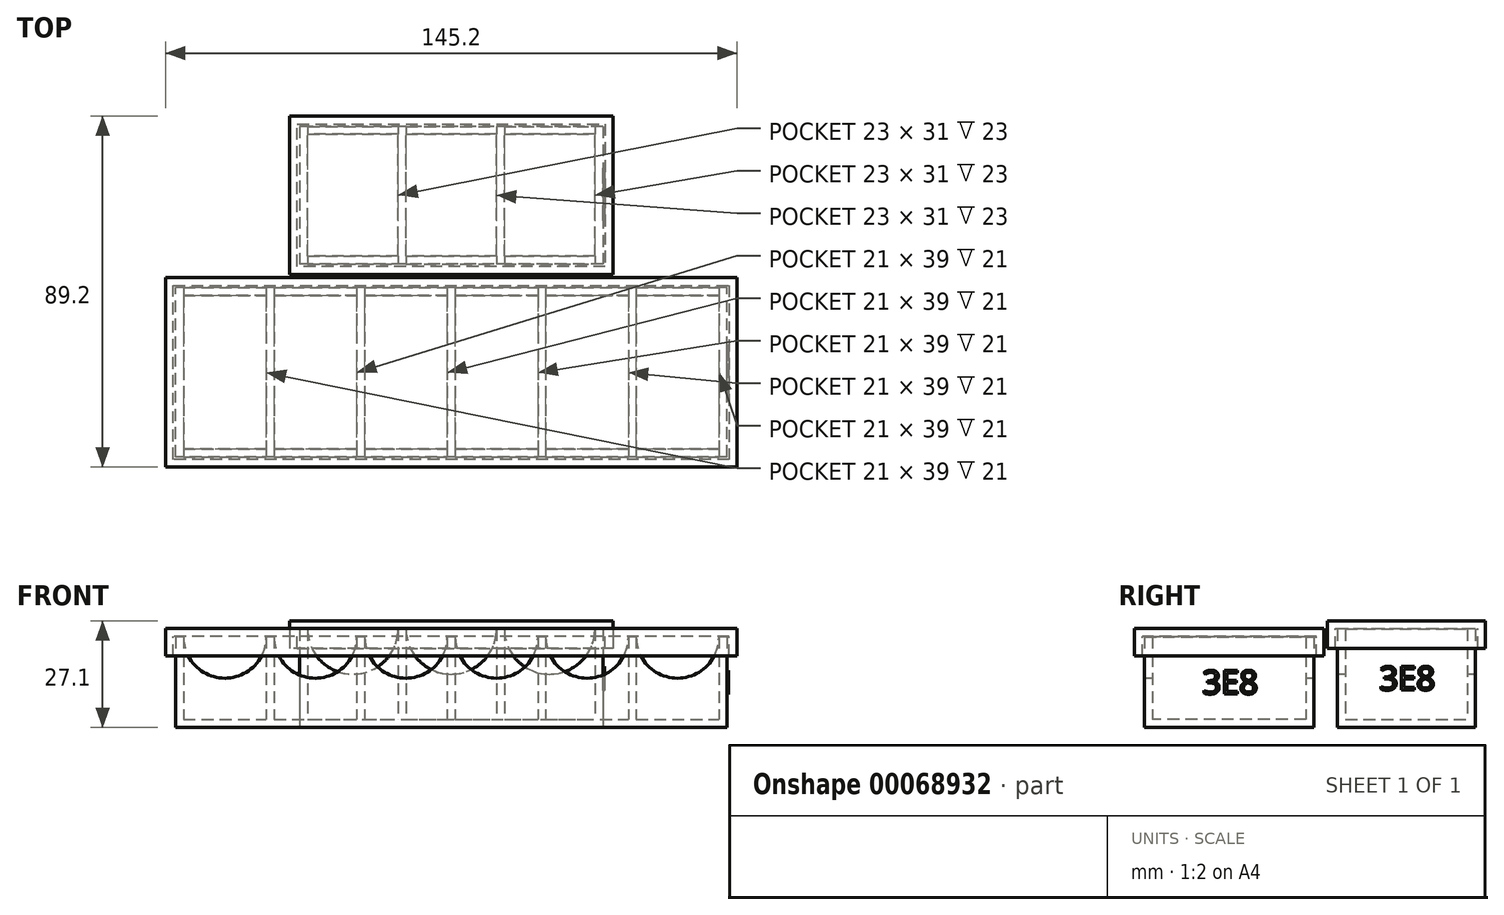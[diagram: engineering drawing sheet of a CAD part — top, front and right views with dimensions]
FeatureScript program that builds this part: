
annotation { "Feature Type Name" : "Feature", "Feature Type Description" : "" }
export const myFeature = defineFeature(function(context is Context, id is Id, definition is map)
    precondition{}
    {
        {
            var Q0;
            Q0=qCreatedBy(makeId("Top.planeOp"),FACE);
            var sketch = newSketch(context, id + "F0", { "sketchPlane" : qUnion([Q0])});
            skLineSegment(sketch, "E0.rect.bottom", {"start": v(70, -21.5) * mm, "end": v(-70, -21.5) * mm});
            skLineSegment(sketch, "E0.rect.top", {"start": v(70, 21.5) * mm, "end": v(-70, 21.5) * mm});
            skLineSegment(sketch, "E0.rect.left", {"start": v(70, -21.5) * mm, "end": v(70, 21.5) * mm});
            skLineSegment(sketch, "E0.rect.right", {"start": v(-70, -21.5) * mm, "end": v(-70, 21.5) * mm});
            skPoint(sketch, "E0.rect.middle", {"position": v(0, 0) * mm});
            skLineSegment(sketch, "E1", {"start": v(0, 0) * mm, "end": v(0, 45) * mm, "construction": true});
            skLineSegment(sketch, "E2.rect.bottom", {"start": v(38.5, 62.5) * mm, "end": v(-38.5, 62.5) * mm});
            skLineSegment(sketch, "E2.rect.top", {"start": v(38.5, 27.5) * mm, "end": v(-38.5, 27.5) * mm});
            skLineSegment(sketch, "E2.rect.left", {"start": v(38.5, 62.5) * mm, "end": v(38.5, 27.5) * mm});
            skLineSegment(sketch, "E2.rect.right", {"start": v(-38.5, 62.5) * mm, "end": v(-38.5, 27.5) * mm});
            skPoint(sketch, "E2.rect.middle", {"position": v(0, 45) * mm});
            skSolve(sketch);
        }
        {
            var Q0;
            Q0 = qSketchRegion(id + "F0", true);
            extrude(context, id + "F1", {"entities" : qUnion([Q0]), "depth" : 2 * mm});
        }
        {
            var Q0;
            Q0=makeQuery(id+"F1.opExtrude","CAP_FACE",FACE,{"disambiguationData":[OSD([sQuery(id+"F0.wireOp",EDGE,"E0.rect.bottom"),sQuery(id+"F0.wireOp",EDGE,"E0.rect.top"),sQuery(id+"F0.wireOp",EDGE,"E0.rect.left"),sQuery(id+"F0.wireOp",EDGE,"E0.rect.right")])],"isStart":false});
            var sketch = newSketch(context, id + "F2", { "sketchPlane" : qUnion([Q0])});
            skLineSegment(sketch, "E3.0.0", {"start": v(-70, -21.5) * mm, "end": v(70, -21.5) * mm});
            skLineSegment(sketch, "E3.0.1", {"start": v(70, -21.5) * mm, "end": v(70, 21.5) * mm});
            skLineSegment(sketch, "E3.0.2", {"start": v(70, 21.5) * mm, "end": v(-70, 21.5) * mm});
            skLineSegment(sketch, "E3.0.3", {"start": v(-70, 21.5) * mm, "end": v(-70, -21.5) * mm});
            skLineSegment(sketch, "E4", {"start": v(-70, 0) * mm, "end": v(-68, 0) * mm, "construction": true});
            skLineSegment(sketch, "E5.bottom", {"start": v(-68, 19.5) * mm, "end": v(-47, 19.5) * mm});
            skLineSegment(sketch, "E5.top", {"start": v(-68, -19.5) * mm, "end": v(-47, -19.5) * mm});
            skLineSegment(sketch, "E5.left", {"start": v(-68, 19.5) * mm, "end": v(-68, -19.5) * mm});
            skLineSegment(sketch, "E5.right", {"start": v(-47, 19.5) * mm, "end": v(-47, -19.5) * mm});
            skLineSegment(sketch, "E6.1.0.0", {"start": v(-24, 19.5) * mm, "end": v(-24, -19.5) * mm});
            skLineSegment(sketch, "E6.1.0.1", {"start": v(-45, 19.5) * mm, "end": v(-24, 19.5) * mm});
            skLineSegment(sketch, "E6.1.0.2", {"start": v(-45, 19.5) * mm, "end": v(-45, -19.5) * mm});
            skLineSegment(sketch, "E6.1.0.3", {"start": v(-45, -19.5) * mm, "end": v(-24, -19.5) * mm});
            skLineSegment(sketch, "E6.2.0.0", {"start": v(-1, 19.5) * mm, "end": v(-1, -19.5) * mm});
            skLineSegment(sketch, "E6.2.0.1", {"start": v(-22, 19.5) * mm, "end": v(-1, 19.5) * mm});
            skLineSegment(sketch, "E6.2.0.2", {"start": v(-22, 19.5) * mm, "end": v(-22, -19.5) * mm});
            skLineSegment(sketch, "E6.2.0.3", {"start": v(-22, -19.5) * mm, "end": v(-1, -19.5) * mm});
            skLineSegment(sketch, "E6.3.0.0", {"start": v(22, 19.5) * mm, "end": v(22, -19.5) * mm});
            skLineSegment(sketch, "E6.3.0.1", {"start": v(1, 19.5) * mm, "end": v(22, 19.5) * mm});
            skLineSegment(sketch, "E6.3.0.2", {"start": v(1, 19.5) * mm, "end": v(1, -19.5) * mm});
            skLineSegment(sketch, "E6.3.0.3", {"start": v(1, -19.5) * mm, "end": v(22, -19.5) * mm});
            skLineSegment(sketch, "E6.4.0.0", {"start": v(45, 19.5) * mm, "end": v(45, -19.5) * mm});
            skLineSegment(sketch, "E6.4.0.1", {"start": v(24, 19.5) * mm, "end": v(45, 19.5) * mm});
            skLineSegment(sketch, "E6.4.0.2", {"start": v(24, 19.5) * mm, "end": v(24, -19.5) * mm});
            skLineSegment(sketch, "E6.4.0.3", {"start": v(24, -19.5) * mm, "end": v(45, -19.5) * mm});
            skLineSegment(sketch, "E6.5.0.0", {"start": v(68, 19.5) * mm, "end": v(68, -19.5) * mm});
            skLineSegment(sketch, "E6.5.0.1", {"start": v(47, 19.5) * mm, "end": v(68, 19.5) * mm});
            skLineSegment(sketch, "E6.5.0.2", {"start": v(47, 19.5) * mm, "end": v(47, -19.5) * mm});
            skLineSegment(sketch, "E6.5.0.3", {"start": v(47, -19.5) * mm, "end": v(68, -19.5) * mm});
            skLineSegment(sketch, "E6.direction1", {"start": v(-47, -19.5) * mm, "end": v(-24, -19.5) * mm, "construction": true});
            skSolve(sketch);
        }
        {
            var Q0;
            Q0 = qSketchRegion(id + "F2", true);
            extrude(context, id + "F3", {"entities" : qUnion([Q0]), "operationType" : NewBodyOperationType.ADD, "depth" : 21 * mm});
        }
        {
            var Q0;
            Q0=makeQuery(id+"F3.boolean.opBoolean","MERGE",FACE,{"derivedFrom":[makeQuery(id+"F1.opExtrude","SWEPT_FACE",FACE,{"disambiguationData":[OSD([sQuery(id+"F0.wireOp",EDGE,"E0.rect.bottom")])]}),makeQuery(id+"F3.opExtrude","SWEPT_FACE",FACE,{"disambiguationData":[OSD([sQuery(id+"F2.wireOp",EDGE,"E3.0.0")])]})]});
            var sketch = newSketch(context, id + "F4", { "sketchPlane" : qUnion([Q0])});
            skPoint(sketch, "E7.0", {"position": v(-68, 23) * mm});
            skPoint(sketch, "E8.0", {"position": v(-47, 23) * mm});
            skLineSegment(sketch, "E9", {"start": v(-68, 23) * mm, "end": v(-47, 23) * mm});
            skArc(sketch, "E10", {"start": v(-68, 23) * mm, "mid": v(-57.5, 12.5) * mm, "end": v(-47, 23) * mm});
            skLineSegment(sketch, "E11.1.0.0", {"start": v(-45, 23) * mm, "end": v(-24, 23) * mm});
            skArc(sketch, "E11.1.0.1", {"start": v(-45, 23) * mm, "mid": v(-34.5, 12.5) * mm, "end": v(-24, 23) * mm});
            skLineSegment(sketch, "E11.2.0.0", {"start": v(-22, 23) * mm, "end": v(-1, 23) * mm});
            skArc(sketch, "E11.2.0.1", {"start": v(-22, 23) * mm, "mid": v(-11.5, 12.5) * mm, "end": v(-1, 23) * mm});
            skLineSegment(sketch, "E11.3.0.0", {"start": v(1, 23) * mm, "end": v(22, 23) * mm});
            skArc(sketch, "E11.3.0.1", {"start": v(1, 23) * mm, "mid": v(11.5, 12.5) * mm, "end": v(22, 23) * mm});
            skLineSegment(sketch, "E11.4.0.0", {"start": v(24, 23) * mm, "end": v(45, 23) * mm});
            skArc(sketch, "E11.4.0.1", {"start": v(24, 23) * mm, "mid": v(34.5, 12.5) * mm, "end": v(45, 23) * mm});
            skLineSegment(sketch, "E11.5.0.0", {"start": v(47, 23) * mm, "end": v(68, 23) * mm});
            skArc(sketch, "E11.5.0.1", {"start": v(47, 23) * mm, "mid": v(57.5, 12.5) * mm, "end": v(68, 23) * mm});
            skLineSegment(sketch, "E11.direction1", {"start": v(-68, 23) * mm, "end": v(-45, 23) * mm, "construction": true});
            skSolve(sketch);
        }
        {
            var Q0;
            Q0 = qSketchRegion(id + "F4", true);
            extrude(context, id + "F5", {"entities" : qUnion([Q0]), "operationType" : NewBodyOperationType.REMOVE, "endBound" : BoundingType.THROUGH_ALL, "oppositeDirection" : true, "depth" : 25 * mm});
        }
        {
            var Q0;
            {var subQ0=sQuery(id+"F2.wireOp",EDGE,"E3.0.0");var subQ1=sQuery(id+"F2.wireOp",EDGE,"E5.bottom");var subQ2=sQuery(id+"F2.wireOp",EDGE,"E3.0.2");var subQ3=sQuery(id+"F2.wireOp",EDGE,"E3.0.3");var subQ4=sQuery(id+"F2.wireOp",EDGE,"E5.top");var subQ5=sQuery(id+"F2.wireOp",EDGE,"E5.left");Q0=makeQuery(id+"F5.boolean.opBoolean","SPLIT",FACE,{"disambiguationData":[TD([makeQuery(id+"F1.opExtrude","SWEPT_FACE",FACE,{"disambiguationData":[OSD([sQuery(id+"F0.wireOp",EDGE,"E0.rect.right")])]})])],"derivedFrom":makeQuery(id+"F3.opExtrude","CAP_FACE",FACE,{"disambiguationData":[OSD([subQ0,sQuery(id+"F2.wireOp",EDGE,"E3.0.1"),subQ2,subQ3,subQ1,subQ4,subQ5,sQuery(id+"F2.wireOp",EDGE,"E5.right"),sQuery(id+"F2.wireOp",EDGE,"E6.1.0.0"),sQuery(id+"F2.wireOp",EDGE,"E6.1.0.1"),sQuery(id+"F2.wireOp",EDGE,"E6.1.0.2"),sQuery(id+"F2.wireOp",EDGE,"E6.1.0.3"),sQuery(id+"F2.wireOp",EDGE,"E6.2.0.0"),sQuery(id+"F2.wireOp",EDGE,"E6.2.0.1"),sQuery(id+"F2.wireOp",EDGE,"E6.2.0.2"),sQuery(id+"F2.wireOp",EDGE,"E6.2.0.3"),sQuery(id+"F2.wireOp",EDGE,"E6.3.0.0"),sQuery(id+"F2.wireOp",EDGE,"E6.3.0.1"),sQuery(id+"F2.wireOp",EDGE,"E6.3.0.2"),sQuery(id+"F2.wireOp",EDGE,"E6.3.0.3"),sQuery(id+"F2.wireOp",EDGE,"E6.4.0.0"),sQuery(id+"F2.wireOp",EDGE,"E6.4.0.1"),sQuery(id+"F2.wireOp",EDGE,"E6.4.0.2"),sQuery(id+"F2.wireOp",EDGE,"E6.4.0.3"),sQuery(id+"F2.wireOp",EDGE,"E6.5.0.0"),sQuery(id+"F2.wireOp",EDGE,"E6.5.0.1"),sQuery(id+"F2.wireOp",EDGE,"E6.5.0.2"),sQuery(id+"F2.wireOp",EDGE,"E6.5.0.3")])],"isStart":false})});}
            cPlane(context, id + "F6", {"entities" : qUnion([Q0]), "cplaneType" : CPlaneType.OFFSET, "offset" : .1 * mm, "width" : 150 * mm, "height" : 150 * mm});
        }
        {
            var Q0;
            Q0=qCreatedBy(id+"F6.planeOp",FACE);
            var sketch = newSketch(context, id + "F7", { "sketchPlane" : qUnion([Q0])});
            skLineSegment(sketch, "E12.0.0", {"start": v(70, -21.5) * mm, "end": v(-70, -21.5) * mm, "construction": true});
            skLineSegment(sketch, "E12.0.1", {"start": v(-70, -21.5) * mm, "end": v(-70, 21.5) * mm, "construction": true});
            skLineSegment(sketch, "E12.0.2", {"start": v(-70, 21.5) * mm, "end": v(70, 21.5) * mm});
            skLineSegment(sketch, "E12.0.3", {"start": v(70, 21.5) * mm, "end": v(70, -21.5) * mm, "construction": true});
            skLineSegment(sketch, "E13.0", {"start": v(-72.6, 24.1) * mm, "end": v(72.6, 24.1) * mm});
            skLineSegment(sketch, "E13.1", {"start": v(-72.6, -24.1) * mm, "end": v(-72.6, 24.1) * mm});
            skLineSegment(sketch, "E13.2", {"start": v(72.6, -24.1) * mm, "end": v(-72.6, -24.1) * mm});
            skLineSegment(sketch, "E13.3", {"start": v(72.6, 24.1) * mm, "end": v(72.6, -24.1) * mm});
            skSolve(sketch);
        }
        {
            var Q0;
            Q0 = qSketchRegion(id + "F7", true);
            extrude(context, id + "F8", {"entities" : qUnion([Q0]), "depth" : 2 * mm});
        }
        {
            var Q0;
            Q0=makeQuery(id+"F8.opExtrude","CAP_FACE",FACE,{"disambiguationData":[OSD([sQuery(id+"F7.wireOp",EDGE,"E13.0"),sQuery(id+"F7.wireOp",EDGE,"E13.1"),sQuery(id+"F7.wireOp",EDGE,"E13.2"),sQuery(id+"F7.wireOp",EDGE,"E13.3")])],"isStart":true});
            var sketch = newSketch(context, id + "F9", { "sketchPlane" : qUnion([Q0])});
            skLineSegment(sketch, "E14.0.0", {"start": v(-72.6, -24.1) * mm, "end": v(72.6, -24.1) * mm});
            skLineSegment(sketch, "E14.0.1", {"start": v(72.6, -24.1) * mm, "end": v(72.6, 24.1) * mm});
            skLineSegment(sketch, "E14.0.2", {"start": v(72.6, 24.1) * mm, "end": v(-72.6, 24.1) * mm});
            skLineSegment(sketch, "E14.0.3", {"start": v(-72.6, 24.1) * mm, "end": v(-72.6, -24.1) * mm});
            skLineSegment(sketch, "E15.0", {"start": v(70.6, 22.1) * mm, "end": v(-70.6, 22.1) * mm});
            skLineSegment(sketch, "E15.1", {"start": v(70.6, -22.1) * mm, "end": v(70.6, 22.1) * mm});
            skLineSegment(sketch, "E15.2", {"start": v(-70.6, -22.1) * mm, "end": v(70.6, -22.1) * mm});
            skLineSegment(sketch, "E15.3", {"start": v(-70.6, 22.1) * mm, "end": v(-70.6, -22.1) * mm});
            skSolve(sketch);
        }
        {
            var Q0;
            Q0 = qSketchRegion(id + "F9", true);
            extrude(context, id + "F10", {"entities" : qUnion([Q0]), "operationType" : NewBodyOperationType.ADD, "depth" : 5 * mm});
        }
        {
            var Q0;
            Q0=makeQuery(id+"F1.opExtrude","CAP_FACE",FACE,{"disambiguationData":[OSD([sQuery(id+"F0.wireOp",EDGE,"E2.rect.bottom"),sQuery(id+"F0.wireOp",EDGE,"E2.rect.top"),sQuery(id+"F0.wireOp",EDGE,"E2.rect.left"),sQuery(id+"F0.wireOp",EDGE,"E2.rect.right")])],"isStart":false});
            var sketch = newSketch(context, id + "F11", { "sketchPlane" : qUnion([Q0])});
            skLineSegment(sketch, "E16.0.0", {"start": v(38.5, 27.5) * mm, "end": v(38.5, 62.5) * mm});
            skLineSegment(sketch, "E16.0.1", {"start": v(38.5, 62.5) * mm, "end": v(-38.5, 62.5) * mm});
            skLineSegment(sketch, "E16.0.2", {"start": v(-38.5, 62.5) * mm, "end": v(-38.5, 27.5) * mm});
            skLineSegment(sketch, "E16.0.3", {"start": v(-38.5, 27.5) * mm, "end": v(38.5, 27.5) * mm});
            skLineSegment(sketch, "E17", {"start": v(-38.5, 45) * mm, "end": v(-36.5, 45) * mm, "construction": true});
            skLineSegment(sketch, "E18.bottom", {"start": v(-36.5, 29.5) * mm, "end": v(-13.5, 29.5) * mm});
            skLineSegment(sketch, "E18.top", {"start": v(-36.5, 60.5) * mm, "end": v(-13.5, 60.5) * mm});
            skLineSegment(sketch, "E18.left", {"start": v(-36.5, 29.5) * mm, "end": v(-36.5, 60.5) * mm});
            skLineSegment(sketch, "E18.right", {"start": v(-13.5, 29.5) * mm, "end": v(-13.5, 60.5) * mm});
            skLineSegment(sketch, "E19.1.0.0", {"start": v(-11.5, 29.5) * mm, "end": v(11.5, 29.5) * mm});
            skLineSegment(sketch, "E19.1.0.1", {"start": v(-11.5, 29.5) * mm, "end": v(-11.5, 60.5) * mm});
            skLineSegment(sketch, "E19.1.0.2", {"start": v(-11.5, 60.5) * mm, "end": v(11.5, 60.5) * mm});
            skLineSegment(sketch, "E19.1.0.3", {"start": v(11.5, 29.5) * mm, "end": v(11.5, 60.5) * mm});
            skLineSegment(sketch, "E19.2.0.0", {"start": v(13.5, 29.5) * mm, "end": v(36.5, 29.5) * mm});
            skLineSegment(sketch, "E19.2.0.1", {"start": v(13.5, 29.5) * mm, "end": v(13.5, 60.5) * mm});
            skLineSegment(sketch, "E19.2.0.2", {"start": v(13.5, 60.5) * mm, "end": v(36.5, 60.5) * mm});
            skLineSegment(sketch, "E19.2.0.3", {"start": v(36.5, 29.5) * mm, "end": v(36.5, 60.5) * mm});
            skLineSegment(sketch, "E19.direction1", {"start": v(-36.5, 29.5) * mm, "end": v(-11.5, 29.5) * mm, "construction": true});
            skSolve(sketch);
        }
        {
            var Q0;
            Q0 = qSketchRegion(id + "F11", true);
            extrude(context, id + "F12", {"entities" : qUnion([Q0]), "operationType" : NewBodyOperationType.ADD, "depth" : 23 * mm});
        }
        {
            var Q0;
            Q0=makeQuery(id+"F12.boolean.opBoolean","MERGE",FACE,{"derivedFrom":[makeQuery(id+"F1.opExtrude","SWEPT_FACE",FACE,{"disambiguationData":[OSD([sQuery(id+"F0.wireOp",EDGE,"E2.rect.top")])]}),makeQuery(id+"F12.opExtrude","SWEPT_FACE",FACE,{"disambiguationData":[OSD([sQuery(id+"F11.wireOp",EDGE,"E16.0.3")])]})]});
            var sketch = newSketch(context, id + "F13", { "sketchPlane" : qUnion([Q0])});
            skPoint(sketch, "E20.0", {"position": v(-36.5, 25) * mm});
            skPoint(sketch, "E21.0", {"position": v(-13.5, 25) * mm});
            skLineSegment(sketch, "E22", {"start": v(-36.5, 25) * mm, "end": v(-13.5, 25) * mm});
            skArc(sketch, "E23", {"start": v(-36.5, 25) * mm, "mid": v(-25, 13.5) * mm, "end": v(-13.5, 25) * mm});
            skArc(sketch, "E24.1.0.0", {"start": v(-11.5, 25) * mm, "mid": v(0, 13.5) * mm, "end": v(11.5, 25) * mm});
            skLineSegment(sketch, "E24.1.0.1", {"start": v(-11.5, 25) * mm, "end": v(11.5, 25) * mm});
            skArc(sketch, "E24.2.0.0", {"start": v(13.5, 25) * mm, "mid": v(25, 13.5) * mm, "end": v(36.5, 25) * mm});
            skLineSegment(sketch, "E24.2.0.1", {"start": v(13.5, 25) * mm, "end": v(36.5, 25) * mm});
            skLineSegment(sketch, "E24.direction1", {"start": v(-36.5, 25) * mm, "end": v(-11.5, 25) * mm, "construction": true});
            skSolve(sketch);
        }
        {
            var Q0;
            Q0 = qSketchRegion(id + "F13", true);
            extrude(context, id + "F14", {"entities" : qUnion([Q0]), "operationType" : NewBodyOperationType.REMOVE, "endBound" : BoundingType.THROUGH_ALL, "oppositeDirection" : true, "depth" : 25 * mm});
        }
        {
            var Q0;
            {var subQ0=sQuery(id+"F11.wireOp",EDGE,"E16.0.1");var subQ1=sQuery(id+"F11.wireOp",EDGE,"E18.bottom");var subQ2=sQuery(id+"F11.wireOp",EDGE,"E18.top");var subQ3=sQuery(id+"F11.wireOp",EDGE,"E18.left");var subQ4=sQuery(id+"F11.wireOp",EDGE,"E16.0.2");var subQ5=sQuery(id+"F11.wireOp",EDGE,"E16.0.3");Q0=makeQuery(id+"F14.boolean.opBoolean","SPLIT",FACE,{"disambiguationData":[TD([makeQuery(id+"F1.opExtrude","SWEPT_FACE",FACE,{"disambiguationData":[OSD([sQuery(id+"F0.wireOp",EDGE,"E2.rect.right")])]})])],"derivedFrom":makeQuery(id+"F12.opExtrude","CAP_FACE",FACE,{"disambiguationData":[OSD([sQuery(id+"F11.wireOp",EDGE,"E16.0.0"),subQ0,subQ4,subQ5,subQ1,subQ2,subQ3,sQuery(id+"F11.wireOp",EDGE,"E18.right"),sQuery(id+"F11.wireOp",EDGE,"E19.1.0.0"),sQuery(id+"F11.wireOp",EDGE,"E19.1.0.1"),sQuery(id+"F11.wireOp",EDGE,"E19.1.0.2"),sQuery(id+"F11.wireOp",EDGE,"E19.1.0.3"),sQuery(id+"F11.wireOp",EDGE,"E19.2.0.0"),sQuery(id+"F11.wireOp",EDGE,"E19.2.0.1"),sQuery(id+"F11.wireOp",EDGE,"E19.2.0.2"),sQuery(id+"F11.wireOp",EDGE,"E19.2.0.3"),sQuery(id+"F11.wireOp",EDGE,"E19.3.0.0"),sQuery(id+"F11.wireOp",EDGE,"E19.3.0.1"),sQuery(id+"F11.wireOp",EDGE,"E19.3.0.2"),sQuery(id+"F11.wireOp",EDGE,"E19.3.0.3")])],"isStart":false})});}
            cPlane(context, id + "F15", {"entities" : qUnion([Q0]), "cplaneType" : CPlaneType.OFFSET, "offset" : .1 * mm, "width" : 150 * mm, "height" : 150 * mm});
        }
        {
            var Q0;
            Q0=qCreatedBy(id+"F15.planeOp",FACE);
            var sketch = newSketch(context, id + "F16", { "sketchPlane" : qUnion([Q0])});
            skLineSegment(sketch, "E25.0.0", {"start": v(38.5, 62.5) * mm, "end": v(38.5, 27.5) * mm, "construction": true});
            skLineSegment(sketch, "E25.0.1", {"start": v(38.5, 27.5) * mm, "end": v(-38.5, 27.5) * mm, "construction": true});
            skLineSegment(sketch, "E25.0.2", {"start": v(-38.5, 27.5) * mm, "end": v(-38.5, 62.5) * mm, "construction": true});
            skLineSegment(sketch, "E25.0.3", {"start": v(-38.5, 62.5) * mm, "end": v(38.5, 62.5) * mm, "construction": true});
            skLineSegment(sketch, "E26.0", {"start": v(-41.1, 24.9) * mm, "end": v(-41.1, 65.1) * mm});
            skLineSegment(sketch, "E26.1", {"start": v(41.1, 24.9) * mm, "end": v(-41.1, 24.9) * mm});
            skLineSegment(sketch, "E26.2", {"start": v(41.1, 65.1) * mm, "end": v(41.1, 24.9) * mm});
            skLineSegment(sketch, "E26.3", {"start": v(-41.1, 65.1) * mm, "end": v(41.1, 65.1) * mm});
            skSolve(sketch);
        }
        {
            var Q0;
            Q0 = qSketchRegion(id + "F16", true);
            extrude(context, id + "F17", {"entities" : qUnion([Q0]), "depth" : 2 * mm});
        }
        {
            var Q0;
            Q0=makeQuery(id+"F17.opExtrude","CAP_FACE",FACE,{"disambiguationData":[OSD([sQuery(id+"F16.wireOp",EDGE,"E26.0"),sQuery(id+"F16.wireOp",EDGE,"E26.1"),sQuery(id+"F16.wireOp",EDGE,"E26.2"),sQuery(id+"F16.wireOp",EDGE,"E26.3")])],"isStart":true});
            var sketch = newSketch(context, id + "F18", { "sketchPlane" : qUnion([Q0])});
            skLineSegment(sketch, "E27.0.0", {"start": v(-41.1, -24.9) * mm, "end": v(-41.1, -65.1) * mm});
            skLineSegment(sketch, "E27.0.1", {"start": v(-41.1, -65.1) * mm, "end": v(41.1, -65.1) * mm});
            skLineSegment(sketch, "E27.0.2", {"start": v(41.1, -65.1) * mm, "end": v(41.1, -24.9) * mm});
            skLineSegment(sketch, "E27.0.3", {"start": v(41.1, -24.9) * mm, "end": v(-41.1, -24.9) * mm});
            skLineSegment(sketch, "E28.0", {"start": v(-39.1, -63.1) * mm, "end": v(39.1, -63.1) * mm});
            skLineSegment(sketch, "E28.1", {"start": v(-39.1, -26.9) * mm, "end": v(-39.1, -63.1) * mm});
            skLineSegment(sketch, "E28.2", {"start": v(39.1, -26.9) * mm, "end": v(-39.1, -26.9) * mm});
            skLineSegment(sketch, "E28.3", {"start": v(39.1, -63.1) * mm, "end": v(39.1, -26.9) * mm});
            skSolve(sketch);
        }
        {
            var Q0;
            Q0 = qSketchRegion(id + "F18", true);
            extrude(context, id + "F19", {"entities" : qUnion([Q0]), "operationType" : NewBodyOperationType.ADD, "depth" : 5 * mm});
        }
        {
            var Q0;
            Q0=makeQuery(id+"F3.boolean.opBoolean","MERGE",FACE,{"derivedFrom":[makeQuery(id+"F1.opExtrude","SWEPT_FACE",FACE,{"disambiguationData":[OSD([sQuery(id+"F0.wireOp",EDGE,"E0.rect.left")])]}),makeQuery(id+"F3.opExtrude","SWEPT_FACE",FACE,{"disambiguationData":[OSD([sQuery(id+"F2.wireOp",EDGE,"E3.0.1")])]})]});
            var sketch = newSketch(context, id + "F20", { "sketchPlane" : qUnion([Q0])});
            skText(sketch, "E29", { "text": "3E8", "fontName": "OpenSans-Regular.ttf"});
            skLineSegment(sketch, "E30", {"start": v(-21.5, 23) * mm, "end": v(21.5, 0) * mm, "construction": true});
            skPoint(sketch, "E31", {"position": v(0, 11.5) * mm});
            const initialGuessF20  = {"E29": [-0.00687, 0.0085, 1, 0, 0.006]};
            skSetInitialGuess(sketch, initialGuessF20);
            skSolve(sketch);
        }
        {
            var Q0;
            Q0 = qSketchRegion(id + "F20", true);
            extrude(context, id + "F21", {"entities" : qUnion([Q0]), "operationType" : NewBodyOperationType.ADD, "depth" : .5 * mm});
        }
        {
            var Q0;
            Q0=makeQuery(id+"F12.boolean.opBoolean","MERGE",FACE,{"derivedFrom":[makeQuery(id+"F1.opExtrude","SWEPT_FACE",FACE,{"disambiguationData":[OSD([sQuery(id+"F0.wireOp",EDGE,"E2.rect.left")])]}),makeQuery(id+"F12.opExtrude","SWEPT_FACE",FACE,{"disambiguationData":[OSD([sQuery(id+"F11.wireOp",EDGE,"E16.0.0")])]})]});
            var sketch = newSketch(context, id + "F22", { "sketchPlane" : qUnion([Q0])});
            skText(sketch, "E32", { "text": "3E8", "fontName": "OpenSans-Regular.ttf"});
            skPoint(sketch, "E33", {"position": v(45, 12.5) * mm});
            skLineSegment(sketch, "E34", {"start": v(27.5, 25) * mm, "end": v(62.5, 0) * mm, "construction": true});
            const initialGuessF22  = {"E32": [0.03813, 0.0095, 1, 0, 0.006]};
            skSetInitialGuess(sketch, initialGuessF22);
            skSolve(sketch);
        }
        {
            var Q0;
            Q0 = qSketchRegion(id + "F22", true);
            extrude(context, id + "F23", {"entities" : qUnion([Q0]), "operationType" : NewBodyOperationType.ADD, "depth" : .5 * mm});
        }
    });
